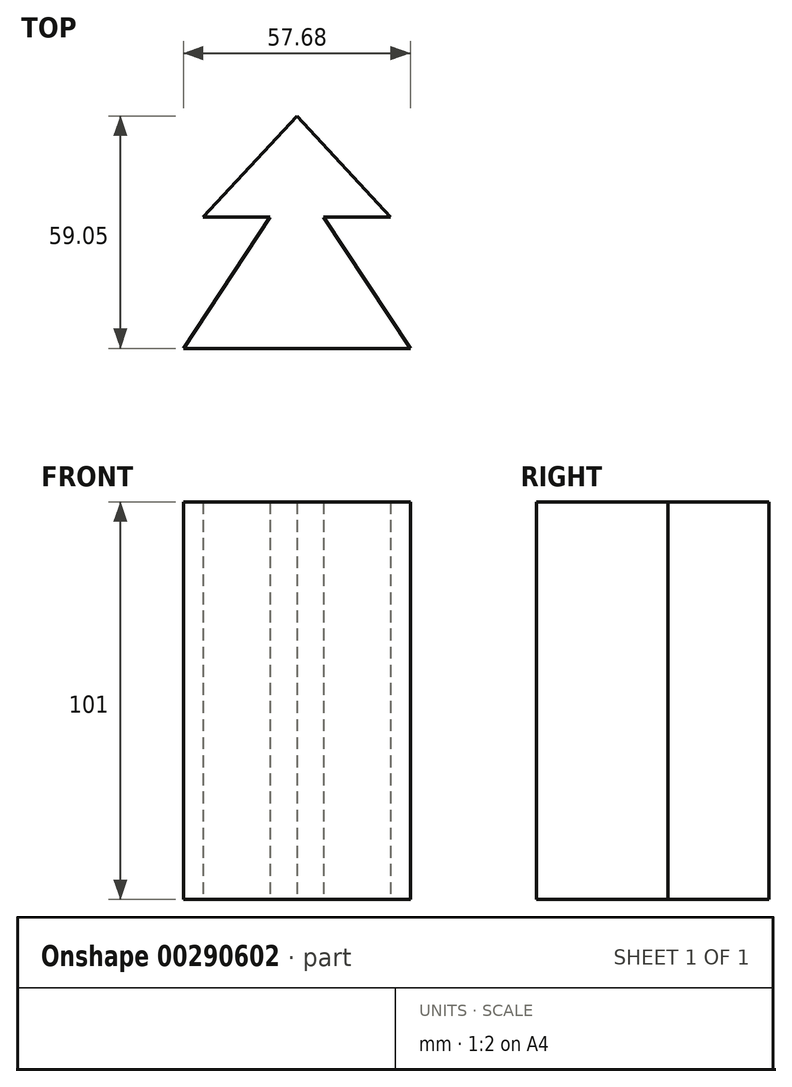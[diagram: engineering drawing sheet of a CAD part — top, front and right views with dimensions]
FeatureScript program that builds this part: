
annotation { "Feature Type Name" : "Feature", "Feature Type Description" : "" }
export const myFeature = defineFeature(function(context is Context, id is Id, definition is map)
    precondition{}
    {
        {
            var Q0;
            Q0=qCreatedBy(makeId("Top.planeOp"),FACE);
            var sketch = newSketch(context, id + "F0", { "sketchPlane" : qUnion([Q0])});
            skLineSegment(sketch, "E0", {"start": v(0, 43.34) * mm, "end": v(-23.8, 17.67) * mm});
            skLineSegment(sketch, "E1", {"start": v(-23.8, 17.67) * mm, "end": v(-6.8, 17.67) * mm});
            skLineSegment(sketch, "E2", {"start": v(-6.8, 17.67) * mm, "end": v(-28.84, -15.7) * mm});
            skLineSegment(sketch, "E3", {"start": v(-28.84, -15.7) * mm, "end": v(28.84, -15.7) * mm});
            skLineSegment(sketch, "E4", {"start": v(28.84, -15.7) * mm, "end": v(6.8, 17.67) * mm});
            skLineSegment(sketch, "E5", {"start": v(6.8, 17.67) * mm, "end": v(23.8, 17.67) * mm});
            skLineSegment(sketch, "E6", {"start": v(23.8, 17.67) * mm, "end": v(0, 43.34) * mm});
            skSolve(sketch);
        }
        {
            var Q0;
            Q0=makeQuery(id+"F0.imprint","IMPRINT",FACE,{"disambiguationData":[TD([[makeQuery(id+"F0.imprint","IMPRINT",EDGE,{"derivedFrom":sQuery(id+"F0.wireOp",EDGE,"E0")}),1.0]])]});
            extrude(context, id + "F1", {"entities" : qUnion([Q0]), "depth" : 101 * mm, "symmetric" : true});
        }
    });
